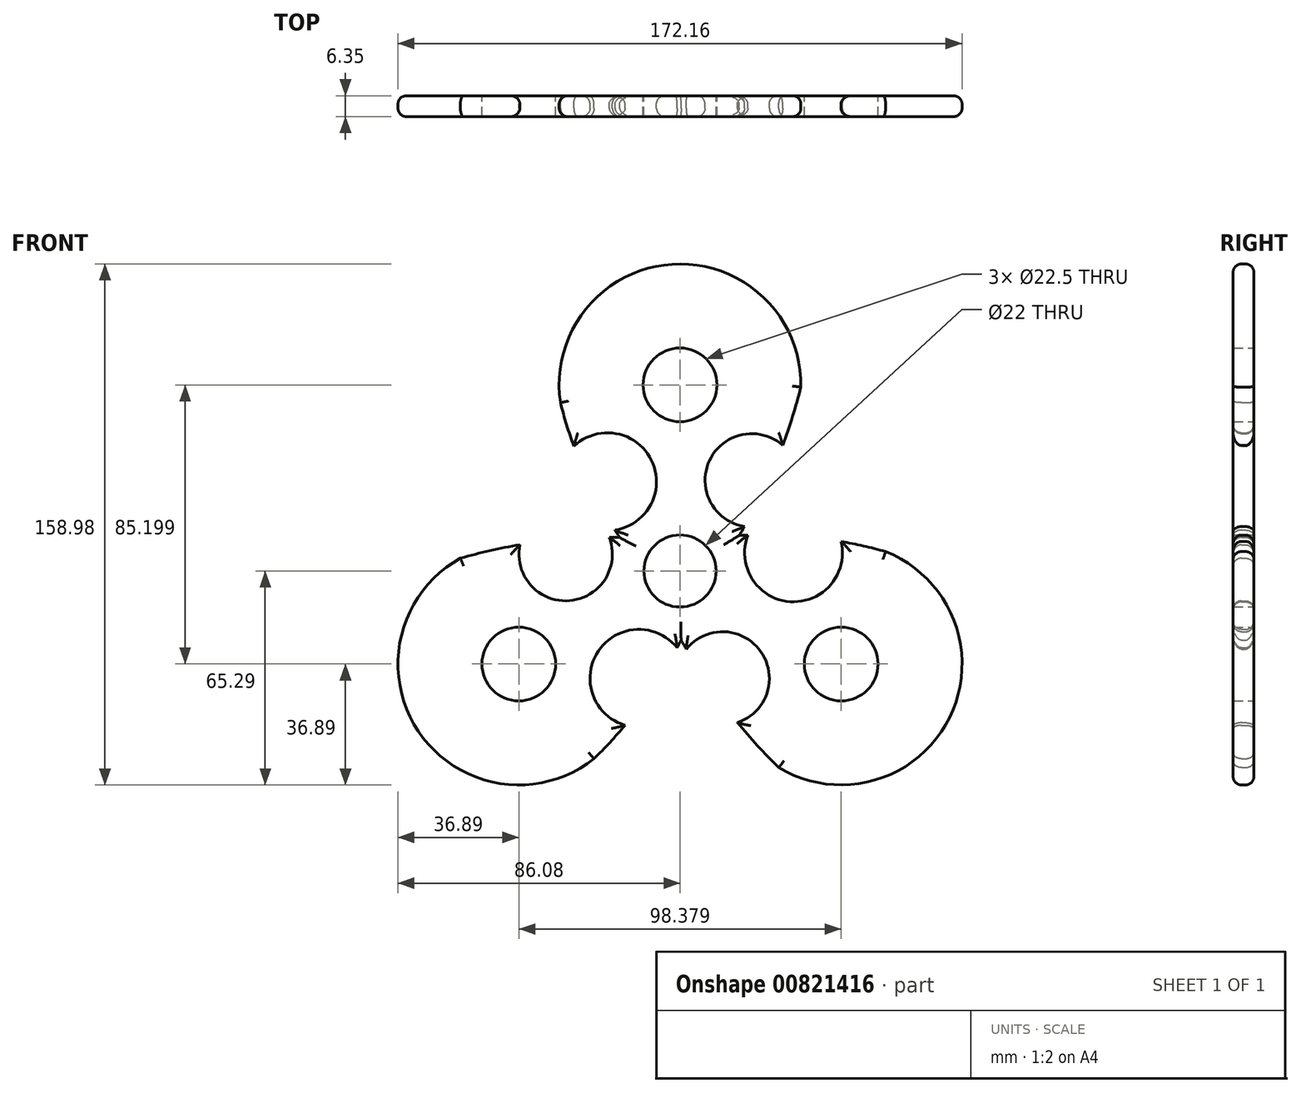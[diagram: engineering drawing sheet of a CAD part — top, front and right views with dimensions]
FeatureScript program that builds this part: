
annotation { "Feature Type Name" : "Feature", "Feature Type Description" : "" }
export const myFeature = defineFeature(function(context is Context, id is Id, definition is map)
    precondition{}
    {
        {
            var Q0;
            Q0=qCreatedBy(makeId("Front.planeOp"),FACE);
            var sketch = newSketch(context, id + "F0", { "sketchPlane" : qUnion([Q0])});
            skCircle(sketch, "E0", {"center": v(0, 0) * mm, "radius": 11 * mm});
            skCircle(sketch, "E1", {"center": v(0, 56.8) * mm, "radius": 11.25 * mm});
            skArc(sketch, "E2", {"start": v(36.89, 56.1) * mm, "mid": v(-2.37, 93.62) * mm, "end": v(-36.5, 51.38) * mm});
            skArc(sketch, "E3", {"start": v(18.1, 10.83) * mm, "mid": v(18.9, 12.2) * mm, "end": v(19.7, 13.57) * mm});
            skArc(sketch, "E4", {"start": v(-36.5, 51.38) * mm, "mid": v(-34.61, 44.67) * mm, "end": v(-32.4, 38.06) * mm});
            skArc(sketch, "E5", {"start": v(-19.86, 12.49) * mm, "mid": v(-8.7, 33.81) * mm, "end": v(-32.4, 38.06) * mm});
            skArc(sketch, "E6", {"start": v(31.35, 38.32) * mm, "mid": v(9, 33.72) * mm, "end": v(19.7, 13.57) * mm});
            skArc(sketch, "E7.trimOffspring", {"start": v(-19.86, 12.49) * mm, "mid": v(-19.15, 11.37) * mm, "end": v(-18.43, 10.25) * mm});
            skArc(sketch, "E8.trimOffspring", {"start": v(31.35, 38.32) * mm, "mid": v(34.36, 47.13) * mm, "end": v(36.89, 56.1) * mm});
            skCircle(sketch, "E9.1.0", {"center": v(-49.19, -28.4) * mm, "radius": 11.25 * mm});
            skArc(sketch, "E9.1.1", {"start": v(-48.86, 7.99) * mm, "mid": v(-58, 6.2) * mm, "end": v(-67.03, 3.9) * mm});
            skArc(sketch, "E9.1.2", {"start": v(-26.25, -57.3) * mm, "mid": v(-21.38, -52.31) * mm, "end": v(-16.77, -47.08) * mm});
            skArc(sketch, "E9.1.3", {"start": v(-67.03, 3.9) * mm, "mid": v(-79.9, -48.86) * mm, "end": v(-26.25, -57.3) * mm});
            skArc(sketch, "E9.1.4", {"start": v(-48.86, 7.99) * mm, "mid": v(-33.7, -9.07) * mm, "end": v(-21.6, 10.27) * mm});
            skArc(sketch, "E9.1.5", {"start": v(-0.88, -23.45) * mm, "mid": v(-24.93, -24.44) * mm, "end": v(-16.77, -47.08) * mm});
            skArc(sketch, "E9.1.6", {"start": v(-0.88, -23.45) * mm, "mid": v(-0.27, -22.27) * mm, "end": v(0.34, -21.08) * mm});
            skArc(sketch, "E9.1.7", {"start": v(-18.43, 10.25) * mm, "mid": v(-20.01, 10.27) * mm, "end": v(-21.6, 10.27) * mm});
            skCircle(sketch, "E9.2.0", {"center": v(49.19, -28.4) * mm, "radius": 11.25 * mm});
            skArc(sketch, "E9.2.1", {"start": v(17.51, -46.3) * mm, "mid": v(23.64, -53.33) * mm, "end": v(30.14, -60) * mm});
            skArc(sketch, "E9.2.2", {"start": v(62.75, 5.91) * mm, "mid": v(56, 7.64) * mm, "end": v(49.16, 9.02) * mm});
            skArc(sketch, "E9.2.3", {"start": v(30.14, -60) * mm, "mid": v(82.26, -44.76) * mm, "end": v(62.75, 5.91) * mm});
            skArc(sketch, "E9.2.4", {"start": v(17.51, -46.3) * mm, "mid": v(24.7, -24.65) * mm, "end": v(1.9, -23.84) * mm});
            skArc(sketch, "E9.2.5", {"start": v(20.75, 10.96) * mm, "mid": v(33.63, -9.37) * mm, "end": v(49.16, 9.02) * mm});
            skArc(sketch, "E9.2.6", {"start": v(20.75, 10.96) * mm, "mid": v(19.42, 10.9) * mm, "end": v(18.1, 10.83) * mm});
            skArc(sketch, "E9.2.7", {"start": v(0.34, -21.08) * mm, "mid": v(1.11, -22.47) * mm, "end": v(1.9, -23.84) * mm});
            skPoint(sketch, "E10.orphan", {"position": v(-11, 0) * mm});
            skPoint(sketch, "E11.orphan", {"position": v(-5.5, 9.53) * mm});
            skPoint(sketch, "E12.orphan", {"position": v(5.5, 9.53) * mm});
            skPoint(sketch, "E13.orphan", {"position": v(11, 0) * mm});
            skPoint(sketch, "E14.orphan", {"position": v(5.5, -9.53) * mm});
            skPoint(sketch, "E15.orphan", {"position": v(-5.5, -9.53) * mm});
            skSolve(sketch);
        }
        {
            var Q0;
            Q0=makeQuery(id+"F0.imprint","IMPRINT",FACE,{"disambiguationData":[TD([[makeQuery(id+"F0.imprint","IMPRINT",EDGE,{"derivedFrom":sQuery(id+"F0.wireOp",EDGE,"E0")}),-1.0]])]});
            extrude(context, id + "F1", {"entities" : qUnion([Q0]), "depth" : 6.35 * mm, "offsetDistance" : 25.4 * mm});
        }
        {
            var Q0;
            Q0=makeQuery(id+"F1.opExtrude","CAP_EDGE",EDGE,{"disambiguationData":[OSD([sQuery(id+"F0.wireOp",EDGE,"E2")])],"isStart":true});
            var Q1;
            Q1=makeQuery(id+"F1.opExtrude","CAP_EDGE",EDGE,{"disambiguationData":[OSD([sQuery(id+"F0.wireOp",EDGE,"E4")])],"isStart":true});
            var Q2;
            Q2=makeQuery(id+"F1.opExtrude","CAP_EDGE",EDGE,{"disambiguationData":[OSD([sQuery(id+"F0.wireOp",EDGE,"E8.trimOffspring")])],"isStart":true});
            var Q3;
            Q3=makeQuery(id+"F1.opExtrude","CAP_EDGE",EDGE,{"disambiguationData":[OSD([sQuery(id+"F0.wireOp",EDGE,"E5")])],"isStart":true});
            var Q4;
            Q4=makeQuery(id+"F1.opExtrude","CAP_EDGE",EDGE,{"disambiguationData":[OSD([sQuery(id+"F0.wireOp",EDGE,"E6")])],"isStart":true});
            var Q5;
            Q5=makeQuery(id+"F1.opExtrude","CAP_EDGE",EDGE,{"disambiguationData":[OSD([sQuery(id+"F0.wireOp",EDGE,"E3")])],"isStart":true});
            var Q6;
            Q6=makeQuery(id+"F1.opExtrude","CAP_EDGE",EDGE,{"disambiguationData":[OSD([sQuery(id+"F0.wireOp",EDGE,"E9.1.7")])],"isStart":true});
            var Q7;
            Q7=makeQuery(id+"F1.opExtrude","CAP_EDGE",EDGE,{"disambiguationData":[OSD([sQuery(id+"F0.wireOp",EDGE,"E7.trimOffspring")])],"isStart":true});
            var Q8;
            Q8=makeQuery(id+"F1.opExtrude","CAP_EDGE",EDGE,{"disambiguationData":[OSD([sQuery(id+"F0.wireOp",EDGE,"E9.1.4")])],"isStart":true});
            var Q9;
            Q9=makeQuery(id+"F1.opExtrude","CAP_EDGE",EDGE,{"disambiguationData":[OSD([sQuery(id+"F0.wireOp",EDGE,"E9.1.1")])],"isStart":true});
            var Q10;
            Q10=makeQuery(id+"F1.opExtrude","CAP_EDGE",EDGE,{"disambiguationData":[OSD([sQuery(id+"F0.wireOp",EDGE,"E9.1.3")])],"isStart":true});
            var Q11;
            Q11=makeQuery(id+"F1.opExtrude","CAP_EDGE",EDGE,{"disambiguationData":[OSD([sQuery(id+"F0.wireOp",EDGE,"E9.1.2")])],"isStart":true});
            var Q12;
            Q12=makeQuery(id+"F1.opExtrude","CAP_EDGE",EDGE,{"disambiguationData":[OSD([sQuery(id+"F0.wireOp",EDGE,"E9.1.5")])],"isStart":true});
            var Q13;
            Q13=makeQuery(id+"F1.opExtrude","CAP_EDGE",EDGE,{"disambiguationData":[OSD([sQuery(id+"F0.wireOp",EDGE,"E9.1.6")])],"isStart":true});
            var Q14;
            Q14=makeQuery(id+"F1.opExtrude","CAP_EDGE",EDGE,{"disambiguationData":[OSD([sQuery(id+"F0.wireOp",EDGE,"E9.2.7")])],"isStart":true});
            var Q15;
            Q15=makeQuery(id+"F1.opExtrude","CAP_EDGE",EDGE,{"disambiguationData":[OSD([sQuery(id+"F0.wireOp",EDGE,"E9.2.4")])],"isStart":true});
            var Q16;
            Q16=makeQuery(id+"F1.opExtrude","CAP_EDGE",EDGE,{"disambiguationData":[OSD([sQuery(id+"F0.wireOp",EDGE,"E9.2.1")])],"isStart":true});
            var Q17;
            Q17=makeQuery(id+"F1.opExtrude","CAP_EDGE",EDGE,{"disambiguationData":[OSD([sQuery(id+"F0.wireOp",EDGE,"E9.2.4")])],"isStart":false});
            var Q18;
            Q18=makeQuery(id+"F1.opExtrude","CAP_EDGE",EDGE,{"disambiguationData":[OSD([sQuery(id+"F0.wireOp",EDGE,"E9.2.1")])],"isStart":false});
            var Q19;
            Q19=makeQuery(id+"F1.opExtrude","CAP_EDGE",EDGE,{"disambiguationData":[OSD([sQuery(id+"F0.wireOp",EDGE,"E9.2.3")])],"isStart":false});
            var Q20;
            Q20=makeQuery(id+"F1.opExtrude","CAP_EDGE",EDGE,{"disambiguationData":[OSD([sQuery(id+"F0.wireOp",EDGE,"E9.2.3")])],"isStart":true});
            var Q21;
            Q21=makeQuery(id+"F1.opExtrude","CAP_EDGE",EDGE,{"disambiguationData":[OSD([sQuery(id+"F0.wireOp",EDGE,"E9.2.2")])],"isStart":true});
            var Q22;
            Q22=makeQuery(id+"F1.opExtrude","CAP_EDGE",EDGE,{"disambiguationData":[OSD([sQuery(id+"F0.wireOp",EDGE,"E9.2.5")])],"isStart":true});
            var Q23;
            Q23=makeQuery(id+"F1.opExtrude","CAP_EDGE",EDGE,{"disambiguationData":[OSD([sQuery(id+"F0.wireOp",EDGE,"E9.2.5")])],"isStart":false});
            var Q24;
            Q24=makeQuery(id+"F1.opExtrude","CAP_EDGE",EDGE,{"disambiguationData":[OSD([sQuery(id+"F0.wireOp",EDGE,"E9.2.6")])],"isStart":true});
            var Q25;
            Q25=makeQuery(id+"F1.opExtrude","CAP_EDGE",EDGE,{"disambiguationData":[OSD([sQuery(id+"F0.wireOp",EDGE,"E9.2.2")])],"isStart":false});
            var Q26;
            Q26=makeQuery(id+"F1.opExtrude","CAP_EDGE",EDGE,{"disambiguationData":[OSD([sQuery(id+"F0.wireOp",EDGE,"E3")])],"isStart":false});
            var Q27;
            Q27=makeQuery(id+"F1.opExtrude","CAP_EDGE",EDGE,{"disambiguationData":[OSD([sQuery(id+"F0.wireOp",EDGE,"E6")])],"isStart":false});
            var Q28;
            Q28=makeQuery(id+"F1.opExtrude","CAP_EDGE",EDGE,{"disambiguationData":[OSD([sQuery(id+"F0.wireOp",EDGE,"E8.trimOffspring")])],"isStart":false});
            var Q29;
            Q29=makeQuery(id+"F1.opExtrude","CAP_EDGE",EDGE,{"disambiguationData":[OSD([sQuery(id+"F0.wireOp",EDGE,"E4")])],"isStart":false});
            var Q30;
            Q30=makeQuery(id+"F1.opExtrude","CAP_EDGE",EDGE,{"disambiguationData":[OSD([sQuery(id+"F0.wireOp",EDGE,"E2")])],"isStart":false});
            var Q31;
            Q31=makeQuery(id+"F1.opExtrude","CAP_EDGE",EDGE,{"disambiguationData":[OSD([sQuery(id+"F0.wireOp",EDGE,"E5")])],"isStart":false});
            var Q32;
            Q32=makeQuery(id+"F1.opExtrude","CAP_EDGE",EDGE,{"disambiguationData":[OSD([sQuery(id+"F0.wireOp",EDGE,"E7.trimOffspring")])],"isStart":false});
            var Q33;
            Q33=makeQuery(id+"F1.opExtrude","CAP_EDGE",EDGE,{"disambiguationData":[OSD([sQuery(id+"F0.wireOp",EDGE,"E9.1.7")])],"isStart":false});
            var Q34;
            Q34=makeQuery(id+"F1.opExtrude","CAP_EDGE",EDGE,{"disambiguationData":[OSD([sQuery(id+"F0.wireOp",EDGE,"E9.1.4")])],"isStart":false});
            var Q35;
            Q35=makeQuery(id+"F1.opExtrude","CAP_EDGE",EDGE,{"disambiguationData":[OSD([sQuery(id+"F0.wireOp",EDGE,"E9.1.1")])],"isStart":false});
            var Q36;
            Q36=makeQuery(id+"F1.opExtrude","CAP_EDGE",EDGE,{"disambiguationData":[OSD([sQuery(id+"F0.wireOp",EDGE,"E9.1.3")])],"isStart":false});
            var Q37;
            Q37=makeQuery(id+"F1.opExtrude","CAP_EDGE",EDGE,{"disambiguationData":[OSD([sQuery(id+"F0.wireOp",EDGE,"E9.1.2")])],"isStart":false});
            var Q38;
            Q38=makeQuery(id+"F1.opExtrude","CAP_EDGE",EDGE,{"disambiguationData":[OSD([sQuery(id+"F0.wireOp",EDGE,"E9.1.5")])],"isStart":false});
            var Q39;
            Q39=makeQuery(id+"F1.opExtrude","CAP_EDGE",EDGE,{"disambiguationData":[OSD([sQuery(id+"F0.wireOp",EDGE,"E9.2.7")])],"isStart":false});
            var Q40;
            Q40=makeQuery(id+"F1.opExtrude","CAP_EDGE",EDGE,{"disambiguationData":[OSD([sQuery(id+"F0.wireOp",EDGE,"E9.1.6")])],"isStart":false});
            var Q41;
            Q41=makeQuery(id+"F1.opExtrude","CAP_EDGE",EDGE,{"disambiguationData":[OSD([sQuery(id+"F0.wireOp",EDGE,"E9.2.6")])],"isStart":false});
            fillet(context, id + "F2", {"entities" : qUnion([Q0, Q1, Q2, Q3, Q4, Q5, Q6, Q7, Q8, Q9, Q10, Q11, Q12, Q13, Q14, Q15, Q16, Q17, Q18, Q19, Q20, Q21, Q22, Q23, Q24, Q25, Q26, Q27, Q28, Q29, Q30, Q31, Q32, Q33, Q34, Q35, Q36, Q37, Q38, Q39, Q40, Q41]), "radius" : 2.54 * mm, "tangentPropagation" : true, "allowEdgeOverflow" : false});
        }
    });
